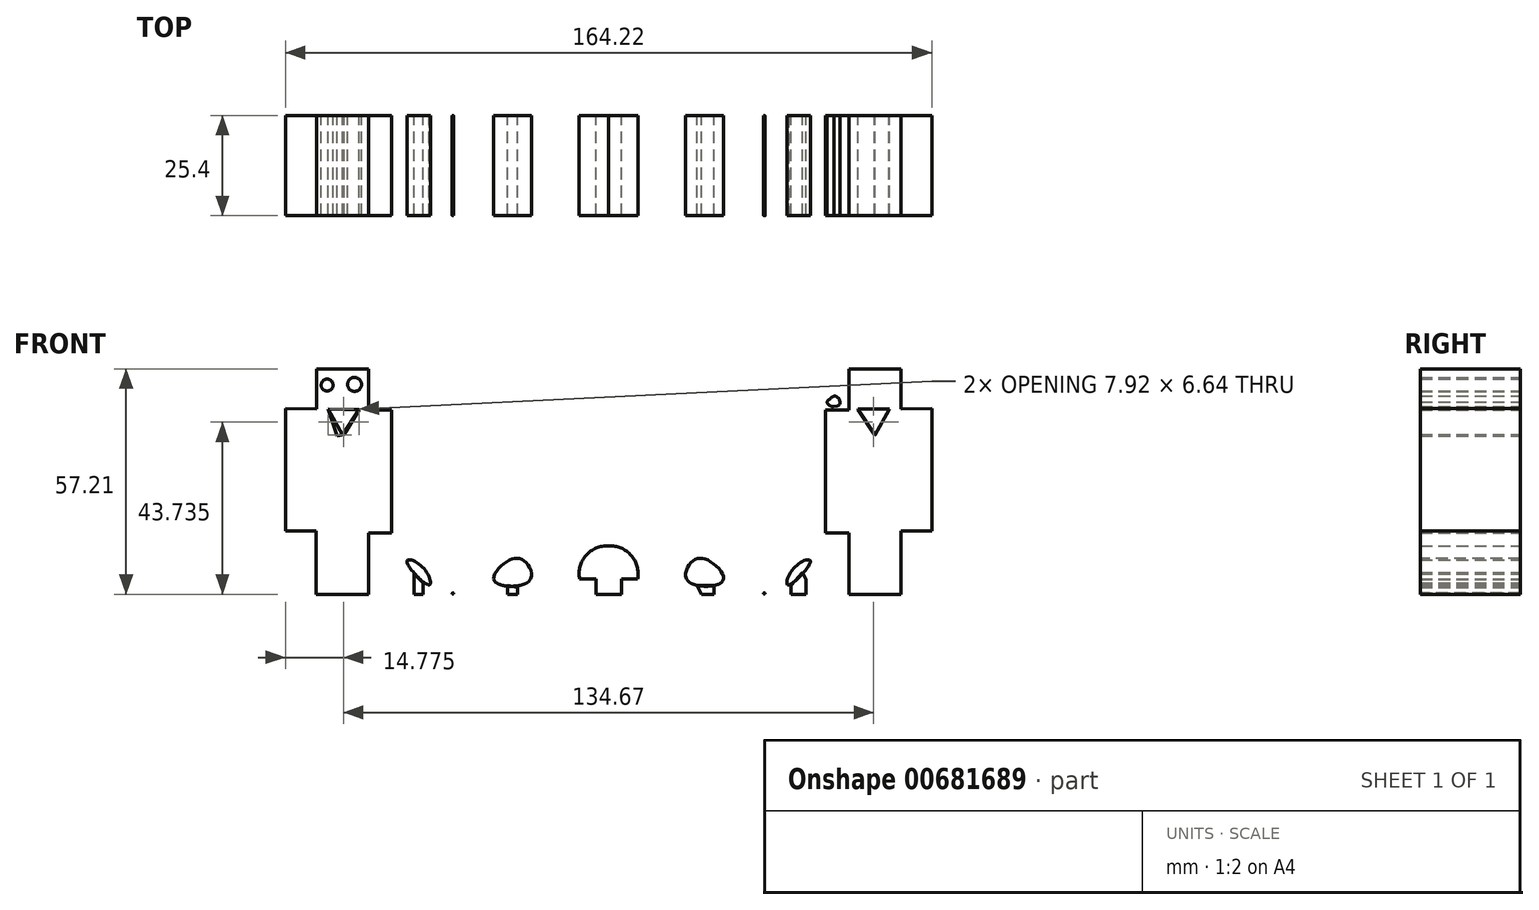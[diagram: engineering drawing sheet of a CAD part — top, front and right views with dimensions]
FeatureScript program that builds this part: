
annotation { "Feature Type Name" : "Feature", "Feature Type Description" : "" }
export const myFeature = defineFeature(function(context is Context, id is Id, definition is map)
    precondition{}
    {
        {
            var Q0;
            Q0=qCreatedBy(makeId("Front.planeOp"),FACE);
            var sketch = newSketch(context, id + "F0", { "sketchPlane" : qUnion([Q0])});
            skLineSegment(sketch, "E0", {"start": v(-75.27, 0) * mm, "end": v(75.95, 0) * mm});
            skLineSegment(sketch, "E1", {"start": v(-3.24, 0) * mm, "end": v(-3.24, 3.86) * mm});
            skLineSegment(sketch, "E2", {"start": v(-3.24, 3.86) * mm, "end": v(-7.36, 3.86) * mm});
            skLineSegment(sketch, "E3.MirrorCS", {"start": v(3.24, 3.86) * mm, "end": v(7.36, 3.86) * mm});
            skLineSegment(sketch, "E4.MirrorCS", {"start": v(3.24, 0) * mm, "end": v(3.24, 3.86) * mm});
            skArc(sketch, "E5", {"start": v(0, 12.3) * mm, "mid": v(-5.73, 9.86) * mm, "end": v(-7.36, 3.86) * mm});
            skArc(sketch, "E6.MirrorCS", {"start": v(0, 12.3) * mm, "mid": v(5.73, 9.86) * mm, "end": v(7.36, 3.86) * mm});
            skSolve(sketch);
        }
        {
            var Q0;
            {var subQ0=sQuery(id+"F0.wireOp",EDGE,"E1");Q0=makeQuery(id+"F0.imprint","IMPRINT",FACE,{"disambiguationData":[TD([[makeQuery(id+"F0.imprint","IMPRINT",EDGE,{"derivedFrom":subQ0}),-1.0]])]});}
            var sketch = newSketch(context, id + "F1", { "sketchPlane" : qUnion([Q0])});
            skLineSegment(sketch, "E7.0.0", {"start": v(-3.24, 0) * mm, "end": v(3.24, 0) * mm});
            skLineSegment(sketch, "E7.0.1", {"start": v(3.24, 0) * mm, "end": v(3.24, 3.86) * mm});
            skLineSegment(sketch, "E7.0.2", {"start": v(3.24, 3.86) * mm, "end": v(7.36, 3.86) * mm});
            skArc(sketch, "E7.0.3", {"start": v(7.36, 3.86) * mm, "mid": v(5.73, 9.86) * mm, "end": v(0, 12.3) * mm});
            skArc(sketch, "E7.0.4", {"start": v(0, 12.3) * mm, "mid": v(-5.73, 9.86) * mm, "end": v(-7.36, 3.86) * mm});
            skLineSegment(sketch, "E7.0.5", {"start": v(-7.36, 3.86) * mm, "end": v(-3.24, 3.86) * mm});
            skLineSegment(sketch, "E7.0.6", {"start": v(-3.24, 3.86) * mm, "end": v(-3.24, 0) * mm});
            skLineSegment(sketch, "E8", {"start": v(-25.5, 0) * mm, "end": v(-25.5, 3.33) * mm});
            skLineSegment(sketch, "E9", {"start": v(-25.5, 3.33) * mm, "end": v(-28.96, 3.33) * mm});
            skLineSegment(sketch, "E10.MirrorCS", {"start": v(25.5, 0) * mm, "end": v(25.5, 3.33) * mm});
            skLineSegment(sketch, "E11.MirrorCS", {"start": v(25.5, 3.33) * mm, "end": v(28.96, 3.33) * mm});
            skLineSegment(sketch, "E12", {"start": v(-22.98, 0) * mm, "end": v(-22.98, 3.33) * mm});
            skLineSegment(sketch, "E13", {"start": v(-22.98, 3.33) * mm, "end": v(-20.19, 3.33) * mm});
            skFitSpline(sketch, "E14", {"points": [v(-28.96, 3.33) * mm, v(-25.78, 8.35) * mm, v(-21.25, 8.35) * mm, v(-20.19, 3.33) * mm, v(-28.96, 3.33) * mm]});
            skLineSegment(sketch, "E15.MirrorCS", {"start": v(22.98, 0) * mm, "end": v(22.98, 3.33) * mm});
            skLineSegment(sketch, "E16.MirrorCS", {"start": v(22.98, 3.33) * mm, "end": v(20.19, 3.33) * mm});
            skFitSpline(sketch, "E17.MirrorC", {"points": [v(28.96, 3.33) * mm, v(25.78, 8.35) * mm, v(21.25, 8.35) * mm, v(20.19, 3.33) * mm, v(28.96, 3.33) * mm]});
            skLineSegment(sketch, "E18", {"start": v(-50.48, 0) * mm, "end": v(-50.48, 2.37) * mm});
            skLineSegment(sketch, "E19", {"start": v(-50.48, 2.37) * mm, "end": v(-53.56, 2.37) * mm});
            skLineSegment(sketch, "E20", {"start": v(-48.26, 0) * mm, "end": v(-48.26, 2.37) * mm});
            skLineSegment(sketch, "E21", {"start": v(-48.26, 2.37) * mm, "end": v(-45.65, 2.37) * mm});
            skArc(sketch, "E22", {"start": v(-51.25, 8.35) * mm, "mid": v(-53.18, 5.65) * mm, "end": v(-53.56, 2.37) * mm});
            skFitSpline(sketch, "E23", {"points": [v(-45.65, 2.37) * mm, v(-47.3, 6.9) * mm, v(-51.25, 8.35) * mm, v(-45.65, 2.37) * mm]});
            skLineSegment(sketch, "E24.MirrorCS", {"start": v(50.48, 0) * mm, "end": v(50.48, 2.37) * mm});
            skLineSegment(sketch, "E25.MirrorCS", {"start": v(50.48, 2.37) * mm, "end": v(53.56, 2.37) * mm});
            skArc(sketch, "E26.MirrorCS", {"start": v(51.25, 8.35) * mm, "mid": v(53.18, 5.65) * mm, "end": v(53.56, 2.37) * mm});
            skFitSpline(sketch, "E27.MirrorC", {"points": [v(45.65, 2.37) * mm, v(47.3, 6.9) * mm, v(51.25, 8.35) * mm, v(45.65, 2.37) * mm]});
            skLineSegment(sketch, "E28.MirrorCS", {"start": v(48.26, 0) * mm, "end": v(48.26, 2.37) * mm});
            skLineSegment(sketch, "E29.MirrorCS", {"start": v(48.26, 2.37) * mm, "end": v(45.65, 2.37) * mm});
            skLineSegment(sketch, "E30", {"start": v(-39.57, 0) * mm, "end": v(-39.57, 0.1) * mm});
            skLineSegment(sketch, "E31", {"start": v(-39.57, 0.1) * mm, "end": v(-39.7, 0.1) * mm});
            skLineSegment(sketch, "E32", {"start": v(-39.46, 0) * mm, "end": v(-39.46, 0.11) * mm});
            skLineSegment(sketch, "E33", {"start": v(-39.46, 0.11) * mm, "end": v(-39.36, 0.11) * mm});
            skArc(sketch, "E34", {"start": v(-39.36, 0.11) * mm, "mid": v(-39.4, 0.25) * mm, "end": v(-39.5, 0.37) * mm});
            skFitSpline(sketch, "E35", {"points": [v(-39.5, 0.37) * mm, v(-39.7, 0.3) * mm, v(-39.7, 0.1) * mm, v(-39.46, 0.11) * mm, v(-39.5, 0.37) * mm]});
            skFitSpline(sketch, "E36.MirrorC", {"points": [v(39.5, 0.37) * mm, v(39.7, 0.3) * mm, v(39.7, 0.1) * mm, v(39.46, 0.11) * mm, v(39.5, 0.37) * mm]});
            skLineSegment(sketch, "E37.MirrorCS", {"start": v(39.57, 0) * mm, "end": v(39.57, 0.1) * mm});
            skLineSegment(sketch, "E38.MirrorCS", {"start": v(39.57, 0.1) * mm, "end": v(39.7, 0.1) * mm});
            skLineSegment(sketch, "E39.MirrorCS", {"start": v(39.46, 0) * mm, "end": v(39.46, 0.11) * mm});
            skLineSegment(sketch, "E40.MirrorCS", {"start": v(39.46, 0.11) * mm, "end": v(39.36, 0.11) * mm});
            skArc(sketch, "E41.MirrorCS", {"start": v(39.36, 0.11) * mm, "mid": v(39.4, 0.25) * mm, "end": v(39.5, 0.37) * mm});
            skSolve(sketch);
        }
        {
            var Q0;
            Q0=qCreatedBy(makeId("Front.planeOp"),FACE);
            var sketch = newSketch(context, id + "F2", { "sketchPlane" : qUnion([Q0])});
            skLineSegment(sketch, "E42", {"start": v(-74.28, 0) * mm, "end": v(-74.28, 16.09) * mm});
            skLineSegment(sketch, "E43", {"start": v(-74.28, 16.09) * mm, "end": v(-82.1, 16.09) * mm});
            skLineSegment(sketch, "E44", {"start": v(-82.1, 16.09) * mm, "end": v(-82.1, 44.62) * mm});
            skLineSegment(sketch, "E45", {"start": v(-61, 57.2) * mm, "end": v(-61, 46.86) * mm});
            skLineSegment(sketch, "E46", {"start": v(-61, 46.86) * mm, "end": v(-55.13, 46.86) * mm});
            skLineSegment(sketch, "E47", {"start": v(-55.13, 46.86) * mm, "end": v(-55.13, 15.53) * mm});
            skLineSegment(sketch, "E48", {"start": v(-55.13, 15.53) * mm, "end": v(-61, 15.53) * mm});
            skLineSegment(sketch, "E49", {"start": v(-61, 15.53) * mm, "end": v(-61, 0) * mm});
            skLineSegment(sketch, "E50", {"start": v(-61, 0) * mm, "end": v(-74.28, 0) * mm});
            skLineSegment(sketch, "E51", {"start": v(-67.64, 0) * mm, "end": v(-67.64, 15.53) * mm});
            skLineSegment(sketch, "E52", {"start": v(-82.1, 44.62) * mm, "end": v(-82.1, 47.14) * mm});
            skLineSegment(sketch, "E53", {"start": v(-61, 57.2) * mm, "end": v(-74.25, 57.2) * mm});
            skLineSegment(sketch, "E54", {"start": v(-74.25, 57.2) * mm, "end": v(-74.25, 47.11) * mm});
            skLineSegment(sketch, "E55", {"start": v(-74.25, 47.11) * mm, "end": v(-82.1, 47.14) * mm});
            skLineSegment(sketch, "E56", {"start": v(-74.25, 47.11) * mm, "end": v(-74.25, 43.29) * mm});
            skLineSegment(sketch, "E57", {"start": v(-61, 46.86) * mm, "end": v(-61, 43.2) * mm});
            skLineSegment(sketch, "E58", {"start": v(-74.25, 47.11) * mm, "end": v(-61, 46.86) * mm});
            skLineSegment(sketch, "E59", {"start": v(-71.3, 47.05) * mm, "end": v(-67.63, 40.42) * mm});
            skPoint(sketch, "E59.endSnap0", {"position": v(-67.63, 46.98) * mm});
            skLineSegment(sketch, "E60", {"start": v(-67.63, 40.42) * mm, "end": v(-63.37, 46.9) * mm});
            skLineSegment(sketch, "E61", {"start": v(-74.28, 16.09) * mm, "end": v(-74.25, 43.29) * mm});
            skLineSegment(sketch, "E62", {"start": v(-61, 43.2) * mm, "end": v(-61, 15.53) * mm});
            skLineSegment(sketch, "E63", {"start": v(-67.64, 15.53) * mm, "end": v(-74.28, 16.09) * mm});
            skLineSegment(sketch, "E64", {"start": v(-67.64, 15.53) * mm, "end": v(-61, 15.53) * mm});
            skLineSegment(sketch, "E65", {"start": v(-67.64, 15.53) * mm, "end": v(-67.63, 40.42) * mm});
            skLineSegment(sketch, "E66", {"start": v(-67.63, 40.42) * mm, "end": v(-67.63, 34.68) * mm});
            skLineSegment(sketch, "E67", {"start": v(-67.63, 29.55) * mm, "end": v(-67.64, 22.85) * mm});
            skLineSegment(sketch, "E68", {"start": v(-67.64, 22.85) * mm, "end": v(-67.64, 15.53) * mm});
            skLineSegment(sketch, "E69.MirrorCS", {"start": v(61, 57.2) * mm, "end": v(74.25, 57.2) * mm});
            skLineSegment(sketch, "E70.MirrorCS", {"start": v(61, 57.2) * mm, "end": v(61, 46.86) * mm});
            skLineSegment(sketch, "E71.MirrorCS", {"start": v(74.25, 57.2) * mm, "end": v(74.25, 47.11) * mm});
            skLineSegment(sketch, "E72.MirrorCS", {"start": v(74.25, 47.11) * mm, "end": v(82.1, 47.14) * mm});
            skLineSegment(sketch, "E73.MirrorCS", {"start": v(82.1, 16.09) * mm, "end": v(82.1, 44.62) * mm});
            skLineSegment(sketch, "E74.MirrorCS", {"start": v(82.1, 44.62) * mm, "end": v(82.1, 47.14) * mm});
            skLineSegment(sketch, "E75.MirrorCS", {"start": v(67.64, 15.53) * mm, "end": v(67.63, 40.42) * mm});
            skLineSegment(sketch, "E76.MirrorCS", {"start": v(67.63, 40.42) * mm, "end": v(63.37, 46.9) * mm});
            skLineSegment(sketch, "E77.MirrorCS", {"start": v(71.3, 47.05) * mm, "end": v(67.63, 40.42) * mm});
            skLineSegment(sketch, "E78.MirrorCS", {"start": v(74.25, 47.11) * mm, "end": v(61, 46.86) * mm});
            skPoint(sketch, "E79.MirrorP", {"position": v(67.63, 46.98) * mm});
            skLineSegment(sketch, "E80.MirrorCS", {"start": v(55.13, 46.86) * mm, "end": v(55.13, 15.53) * mm});
            skLineSegment(sketch, "E81.MirrorCS", {"start": v(61, 43.2) * mm, "end": v(61, 15.53) * mm});
            skLineSegment(sketch, "E82.MirrorCS", {"start": v(55.13, 15.53) * mm, "end": v(61, 15.53) * mm});
            skLineSegment(sketch, "E83.MirrorCS", {"start": v(61, 15.53) * mm, "end": v(61, 0) * mm});
            skLineSegment(sketch, "E84.MirrorCS", {"start": v(67.64, 0) * mm, "end": v(67.64, 15.53) * mm});
            skLineSegment(sketch, "E85.MirrorCS", {"start": v(74.28, 0) * mm, "end": v(74.28, 16.09) * mm});
            skLineSegment(sketch, "E86.MirrorCS", {"start": v(74.28, 16.09) * mm, "end": v(74.25, 43.29) * mm});
            skLineSegment(sketch, "E87.MirrorCS", {"start": v(61, 46.86) * mm, "end": v(55.13, 46.86) * mm});
            skLineSegment(sketch, "E88.MirrorCS", {"start": v(67.64, 15.53) * mm, "end": v(74.28, 16.09) * mm});
            skLineSegment(sketch, "E89.MirrorCS", {"start": v(67.64, 15.53) * mm, "end": v(61, 15.53) * mm});
            skLineSegment(sketch, "E90.MirrorCS", {"start": v(74.28, 16.09) * mm, "end": v(82.1, 16.09) * mm});
            skLineSegment(sketch, "E91.MirrorCS", {"start": v(61, 0) * mm, "end": v(74.28, 0) * mm});
            skLineSegment(sketch, "E92.MirrorCS", {"start": v(74.25, 47.11) * mm, "end": v(74.25, 43.29) * mm});
            skLineSegment(sketch, "E93.MirrorCS", {"start": v(61, 46.86) * mm, "end": v(61, 43.2) * mm});
            skSolve(sketch);
        }
        {
            var Q0;
            Q0 = qSketchRegion(id + "F2", true);
            var Q1;
            Q1 = qSketchRegion(id + "F1", true);
            var Q2;
            Q2 = qSketchRegion(id + "F0", true);
            extrude(context, id + "F3", {"entities" : qUnion([Q0, Q1, Q2]), "depth" : 25.4 * mm, "offsetDistance" : 25.4 * mm});
        }
        {
            var Q0;
            Q0=qCreatedBy(makeId("Front.planeOp"),FACE);
            var sketch = newSketch(context, id + "F4", { "sketchPlane" : qUnion([Q0])});
            skLineSegment(sketch, "E94", {"start": v(-67.7, 40.63) * mm, "end": v(-67.7, 16.34) * mm});
            skLineSegment(sketch, "E95", {"start": v(-74.34, 47.1) * mm, "end": v(-71.02, 47.1) * mm});
            skLineSegment(sketch, "E96", {"start": v(-63.56, 46.93) * mm, "end": v(-61, 46.93) * mm});
            skLineSegment(sketch, "E97", {"start": v(-61, 46.93) * mm, "end": v(-61, 15.43) * mm});
            skLineSegment(sketch, "E98", {"start": v(-74.34, 47.1) * mm, "end": v(-74.34, 16.34) * mm});
            skCircle(sketch, "E99", {"center": v(-71.52, 53.14) * mm, "radius": 1.51 * mm});
            skCircle(sketch, "E100", {"center": v(-64.56, 53.31) * mm, "radius": 1.77 * mm});
            skLineSegment(sketch, "E101.MirrorCS", {"start": v(61, 46.93) * mm, "end": v(61, 15.43) * mm});
            skLineSegment(sketch, "E102.MirrorCS", {"start": v(67.7, 40.63) * mm, "end": v(67.7, 16.34) * mm});
            skLineSegment(sketch, "E103.MirrorCS", {"start": v(74.34, 47.1) * mm, "end": v(74.34, 16.34) * mm});
            skCircle(sketch, "E104.MirrorC", {"center": v(71.52, 53.14) * mm, "radius": 1.51 * mm});
            skCircle(sketch, "E105.MirrorC", {"center": v(64.56, 53.31) * mm, "radius": 1.77 * mm});
            skLineSegment(sketch, "E106.MirrorCS", {"start": v(74.34, 47.1) * mm, "end": v(71.02, 47.1) * mm});
            skLineSegment(sketch, "E107.MirrorCS", {"start": v(63.56, 46.93) * mm, "end": v(61, 46.93) * mm});
            skLineSegment(sketch, "E108", {"start": v(-67.7, 16.34) * mm, "end": v(-67.7, 0) * mm});
            skLineSegment(sketch, "E109", {"start": v(-74.34, 16.34) * mm, "end": v(-67.7, 16.34) * mm});
            skLineSegment(sketch, "E110", {"start": v(-61, 15.43) * mm, "end": v(-67.7, 16.34) * mm});
            skLineSegment(sketch, "E111.MirrorCS", {"start": v(67.7, 16.34) * mm, "end": v(67.7, 0) * mm});
            skLineSegment(sketch, "E112.MirrorCS", {"start": v(74.34, 16.34) * mm, "end": v(67.7, 16.34) * mm});
            skLineSegment(sketch, "E113.MirrorCS", {"start": v(61, 15.43) * mm, "end": v(67.7, 16.34) * mm});
            skLineSegment(sketch, "E114", {"start": v(-49.37, 5.2) * mm, "end": v(-49.37, 0) * mm});
            skLineSegment(sketch, "E115", {"start": v(-49.37, 0) * mm, "end": v(-47.16, 0) * mm});
            skLineSegment(sketch, "E116", {"start": v(-47.16, 0) * mm, "end": v(-47.16, 2.87) * mm});
            skLineSegment(sketch, "E117", {"start": v(-25.65, 2.25) * mm, "end": v(-25.65, 0) * mm});
            skLineSegment(sketch, "E118", {"start": v(-25.65, 0) * mm, "end": v(-23.19, 0) * mm});
            skLineSegment(sketch, "E119", {"start": v(-23.19, 0) * mm, "end": v(-23.19, 1.73) * mm});
            skLineSegment(sketch, "E120", {"start": v(-23.19, 1.73) * mm, "end": v(-25.65, 2.25) * mm});
            skLineSegment(sketch, "E121", {"start": v(22.4, 2.25) * mm, "end": v(23.57, 0) * mm});
            skLineSegment(sketch, "E122", {"start": v(23.57, 0) * mm, "end": v(26.82, 0) * mm});
            skLineSegment(sketch, "E123", {"start": v(26.82, 0) * mm, "end": v(26.82, 2.25) * mm});
            skLineSegment(sketch, "E124", {"start": v(26.82, 2.25) * mm, "end": v(22.4, 2.25) * mm});
            skLineSegment(sketch, "E125", {"start": v(46.3, 2.25) * mm, "end": v(46.3, 0) * mm});
            skLineSegment(sketch, "E126", {"start": v(46.3, 0) * mm, "end": v(50.2, 0) * mm});
            skLineSegment(sketch, "E127", {"start": v(50.2, 0) * mm, "end": v(50.2, 3.8) * mm});
            skLineSegment(sketch, "E128", {"start": v(50.2, 3.8) * mm, "end": v(46.3, 2.25) * mm});
            skLineSegment(sketch, "E129", {"start": v(50.2, 3.8) * mm, "end": v(49.3, 5.52) * mm});
            skLineSegment(sketch, "E130", {"start": v(49.3, 5.52) * mm, "end": v(46.3, 2.25) * mm});
            skLineSegment(sketch, "E131", {"start": v(-49.37, 5.2) * mm, "end": v(-47.16, 2.87) * mm});
            skSolve(sketch);
        }
        {
            var Q0;
            Q0=makeQuery(id+"F4.imprint","IMPRINT",FACE,{"disambiguationData":[TD([[makeQuery(id+"F4.imprint","IMPRINT",EDGE,{"derivedFrom":sQuery(id+"F4.wireOp",EDGE,"E99")}),1.0]])]});
            var Q1;
            Q1=makeQuery(id+"F4.imprint","IMPRINT",FACE,{"disambiguationData":[TD([[makeQuery(id+"F4.imprint","IMPRINT",EDGE,{"derivedFrom":sQuery(id+"F4.wireOp",EDGE,"E100")}),1.0]])]});
            var Q2;
            Q2=makeQuery(id+"F4.imprint","IMPRINT",FACE,{"disambiguationData":[TD([[makeQuery(id+"F4.imprint","IMPRINT",EDGE,{"derivedFrom":sQuery(id+"F4.wireOp",EDGE,"E104.MirrorC")}),-1.0]])]});
            var Q3;
            Q3=makeQuery(id+"F4.imprint","IMPRINT",FACE,{"disambiguationData":[TD([[makeQuery(id+"F4.imprint","IMPRINT",EDGE,{"derivedFrom":sQuery(id+"F4.wireOp",EDGE,"E105.MirrorC")}),-1.0]])]});
            var Q4;
            Q4=makeQuery(id+"F4.imprint","IMPRINT",FACE,{"disambiguationData":[TD([[makeQuery(id+"F4.imprint","IMPRINT",EDGE,{"derivedFrom":sQuery(id+"F4.wireOp",EDGE,"E117")}),1.0]])]});
            var Q5;
            Q5=makeQuery(id+"F4.imprint","IMPRINT",FACE,{"disambiguationData":[TD([[makeQuery(id+"F4.imprint","IMPRINT",EDGE,{"derivedFrom":sQuery(id+"F4.wireOp",EDGE,"E121")}),1.0]])]});
            var Q6;
            Q6=makeQuery(id+"F4.imprint","IMPRINT",FACE,{"disambiguationData":[TD([[makeQuery(id+"F4.imprint","IMPRINT",EDGE,{"derivedFrom":sQuery(id+"F4.wireOp",EDGE,"E125")}),1.0]])]});
            var Q7;
            Q7=makeQuery(id+"F4.imprint","IMPRINT",FACE,{"disambiguationData":[TD([[makeQuery(id+"F4.imprint","IMPRINT",EDGE,{"derivedFrom":sQuery(id+"F4.wireOp",EDGE,"E128")}),-1.0]])]});
            var Q8;
            Q8=makeQuery(id+"F4.imprint","IMPRINT",FACE,{"disambiguationData":[TD([[makeQuery(id+"F4.imprint","IMPRINT",EDGE,{"derivedFrom":sQuery(id+"F4.wireOp",EDGE,"E114")}),1.0]])]});
            extrude(context, id + "F5", {"entities" : qUnion([Q0, Q1, Q2, Q3, Q4, Q5, Q6, Q7, Q8]), "depth" : 25.4 * mm, "offsetDistance" : 25.4 * mm});
        }
        {
            var Q0;
            Q0=qCreatedBy(makeId("Front.planeOp"),FACE);
            var sketch = newSketch(context, id + "F6", { "sketchPlane" : qUnion([Q0])});
            skLineSegment(sketch, "E132", {"start": v(-71.26, 47.12) * mm, "end": v(-63.36, 46.86) * mm});
            skLineSegment(sketch, "E133", {"start": v(-63.36, 46.86) * mm, "end": v(-67.18, 40.53) * mm});
            skLineSegment(sketch, "E134", {"start": v(-67.18, 40.53) * mm, "end": v(-68.94, 40.27) * mm});
            skLineSegment(sketch, "E135", {"start": v(-68.94, 40.27) * mm, "end": v(-71.26, 47.12) * mm});
            skLineSegment(sketch, "E136", {"start": v(63.36, 47.12) * mm, "end": v(71.16, 47.12) * mm});
            skLineSegment(sketch, "E137", {"start": v(71.16, 47.12) * mm, "end": v(71.3, 47.12) * mm});
            skLineSegment(sketch, "E138", {"start": v(71.3, 47.12) * mm, "end": v(71.38, 47.1) * mm});
            skLineSegment(sketch, "E139", {"start": v(71.38, 47.1) * mm, "end": v(71.18, 46.82) * mm});
            skLineSegment(sketch, "E140", {"start": v(71.18, 46.82) * mm, "end": v(67.64, 40.44) * mm});
            skLineSegment(sketch, "E141", {"start": v(67.64, 40.44) * mm, "end": v(67.57, 40.32) * mm});
            skLineSegment(sketch, "E142", {"start": v(67.57, 40.32) * mm, "end": v(67.57, 40.53) * mm});
            skLineSegment(sketch, "E143", {"start": v(67.57, 40.53) * mm, "end": v(63.36, 46.94) * mm});
            skLineSegment(sketch, "E144", {"start": v(63.36, 46.94) * mm, "end": v(63.36, 47.12) * mm});
            skSolve(sketch);
        }
        {
            var Q0;
            Q0=makeQuery(id+"F6.imprint","IMPRINT",FACE,{"disambiguationData":[TD([[makeQuery(id+"F6.imprint","IMPRINT",EDGE,{"derivedFrom":sQuery(id+"F6.wireOp",EDGE,"E136")}),-1.0]])]});
            var Q1;
            Q1=makeQuery(id+"F6.imprint","IMPRINT",FACE,{"disambiguationData":[TD([[makeQuery(id+"F6.imprint","IMPRINT",EDGE,{"derivedFrom":sQuery(id+"F6.wireOp",EDGE,"E132")}),-1.0]])]});
            extrude(context, id + "F7", {"entities" : qUnion([Q0, Q1]), "depth" : 25.4 * mm, "offsetDistance" : 25.4 * mm});
        }
        {
            var Q0;
            Q0=qCreatedBy(makeId("Front.planeOp"),FACE);
            var sketch = newSketch(context, id + "F8", { "sketchPlane" : qUnion([Q0])});
            skLineSegment(sketch, "E145", {"start": v(-58.1, 46.99) * mm, "end": v(-58.1, 47.86) * mm});
            skLineSegment(sketch, "E146", {"start": v(-58.1, 47.86) * mm, "end": v(-57.15, 47.72) * mm});
            skLineSegment(sketch, "E147", {"start": v(-57.15, 47.72) * mm, "end": v(-57.28, 46.85) * mm});
            skLineSegment(sketch, "E148", {"start": v(-57.28, 46.85) * mm, "end": v(-58.1, 46.99) * mm});
            skArc(sketch, "E149", {"start": v(-58.75, 48.88) * mm, "mid": v(-58.65, 48.23) * mm, "end": v(-58.1, 47.86) * mm});
            skArc(sketch, "E150", {"start": v(-57.3, 50.34) * mm, "mid": v(-58.3, 49.9) * mm, "end": v(-58.75, 48.88) * mm});
            skArc(sketch, "E151", {"start": v(-55.47, 48.88) * mm, "mid": v(-56.3, 49.7) * mm, "end": v(-57.3, 50.34) * mm});
            skArc(sketch, "E152", {"start": v(-57.15, 47.72) * mm, "mid": v(-56.07, 47.97) * mm, "end": v(-55.47, 48.88) * mm});
            skLineSegment(sketch, "E153.MirrorCS", {"start": v(57.28, 46.85) * mm, "end": v(58.1, 46.99) * mm});
            skLineSegment(sketch, "E154.MirrorCS", {"start": v(58.1, 46.99) * mm, "end": v(58.1, 47.86) * mm});
            skLineSegment(sketch, "E155.MirrorCS", {"start": v(58.1, 47.86) * mm, "end": v(57.15, 47.72) * mm});
            skArc(sketch, "E156.MirrorCS", {"start": v(58.75, 48.88) * mm, "mid": v(58.65, 48.23) * mm, "end": v(58.1, 47.86) * mm});
            skArc(sketch, "E157.MirrorCS", {"start": v(57.15, 47.72) * mm, "mid": v(56.07, 47.97) * mm, "end": v(55.47, 48.88) * mm});
            skArc(sketch, "E158.MirrorCS", {"start": v(55.47, 48.88) * mm, "mid": v(56.3, 49.7) * mm, "end": v(57.3, 50.34) * mm});
            skArc(sketch, "E159.MirrorCS", {"start": v(57.3, 50.34) * mm, "mid": v(58.3, 49.9) * mm, "end": v(58.75, 48.88) * mm});
            skSolve(sketch);
        }
        {
            var Q0;
            Q0=makeQuery(id+"F8.imprint","IMPRINT",FACE,{"disambiguationData":[TD([[makeQuery(id+"F8.imprint","IMPRINT",EDGE,{"derivedFrom":sQuery(id+"F8.wireOp",EDGE,"E155.MirrorCS")}),-1.0]])]});
            extrude(context, id + "F9", {"entities" : qUnion([Q0]), "depth" : 25.4 * mm, "offsetDistance" : 25.4 * mm});
        }
    });
